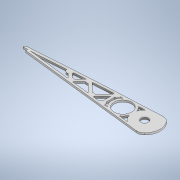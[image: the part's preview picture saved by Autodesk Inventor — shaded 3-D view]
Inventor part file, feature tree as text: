
AUTODESK INVENTOR PART (.ipt)
format: ipt  version: 2022 (Build 260153000, 153)  size: 354,816 bytes
history: native  units: mm
features: extrude x1, sketch x1
ambient origin geometry x8: Origin, YZ Plane, XZ Plane, XY Plane, X Axis, Y Axis, Z Axis, Center Point
bodies: Body1 (feature_tree)
feature tree (2):
  extrude  "Extrusion5"  Depth=10.0mm
  sketch  "Sketch1"  dims[d31=34.456mm d50=368.759386mm d57=16.0mm d69=8.0mm d70=23.0mm d71=8.0mm d73=16.0mm d80=19.0mm d81=16.0mm d82=1.0mm d83=1.0mm d84=1.0mm d85=1.0mm d86=1.0mm d87=0.8mm d88=1.0mm d90=19.0mm d94=5.0mm d95=5.0mm d105=5.0mm d106=5.0mm d108=2.0mm d109=19.0mm d114=5.0mm d115=5.0mm d116=24.0mm d117=2.5mm d118=2.5mm d123=2.5mm d124=2.5mm d125=10.0mm d126=24.0mm d127=24.0mm d128=27.0mm d135=0.5mm d136=45.0deg d139=7.0mm d165=45.0deg d169=27.0mm d175=90.0deg d181=45.0deg d185=7.0mm d186=45.0deg d190=7.0mm d191=45.0deg d197=90.0deg d203=90.0deg d206=7.0mm d207=2.0mm d208=0.0mm]
